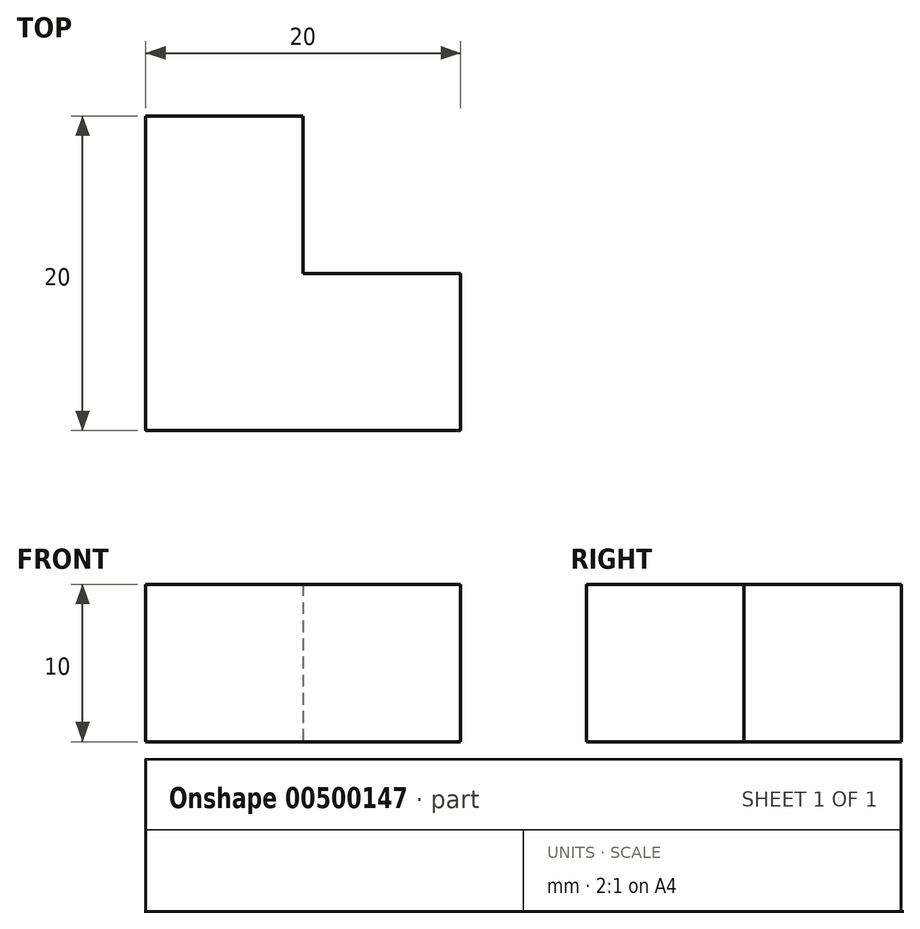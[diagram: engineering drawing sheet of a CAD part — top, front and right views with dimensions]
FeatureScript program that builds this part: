
annotation { "Feature Type Name" : "Feature", "Feature Type Description" : "" }
export const myFeature = defineFeature(function(context is Context, id is Id, definition is map)
    precondition{}
    {
        {
            var Q0;
            Q0=qCreatedBy(makeId("Top.planeOp"),FACE);
            var sketch = newSketch(context, id + "F0", { "sketchPlane" : qUnion([Q0])});
            skLineSegment(sketch, "E0", {"start": v(0, 0) * mm, "end": v(0, 20) * mm});
            skLineSegment(sketch, "E1", {"start": v(0, 20) * mm, "end": v(10, 20) * mm});
            skLineSegment(sketch, "E2", {"start": v(10, 20) * mm, "end": v(10, 10) * mm});
            skLineSegment(sketch, "E3", {"start": v(10, 10) * mm, "end": v(20, 10) * mm});
            skLineSegment(sketch, "E4", {"start": v(20, 10) * mm, "end": v(20, 0) * mm});
            skLineSegment(sketch, "E5", {"start": v(20, 0) * mm, "end": v(0, 0) * mm});
            skSolve(sketch);
        }
        {
            var Q0;
            Q0=makeQuery(id+"F0.imprint","IMPRINT",FACE,{"disambiguationData":[TD([[makeQuery(id+"F0.imprint","IMPRINT",EDGE,{"derivedFrom":sQuery(id+"F0.wireOp",EDGE,"E0")}),-1.0]])]});
            var sketch = newSketch(context, id + "F1", { "sketchPlane" : qUnion([Q0])});
            skSolve(sketch);
        }
        {
            var Q0;
            Q0 = qSketchRegion(id + "F1", true);
            var Q1;
            Q1=makeQuery(id+"F0.imprint","IMPRINT",FACE,{"disambiguationData":[TD([[makeQuery(id+"F0.imprint","IMPRINT",EDGE,{"derivedFrom":sQuery(id+"F0.wireOp",EDGE,"E0")}),-1.0]])]});
            extrude(context, id + "F2", {"entities" : qUnion([Q0, Q1]), "depth" : 10 * mm});
        }
    });
